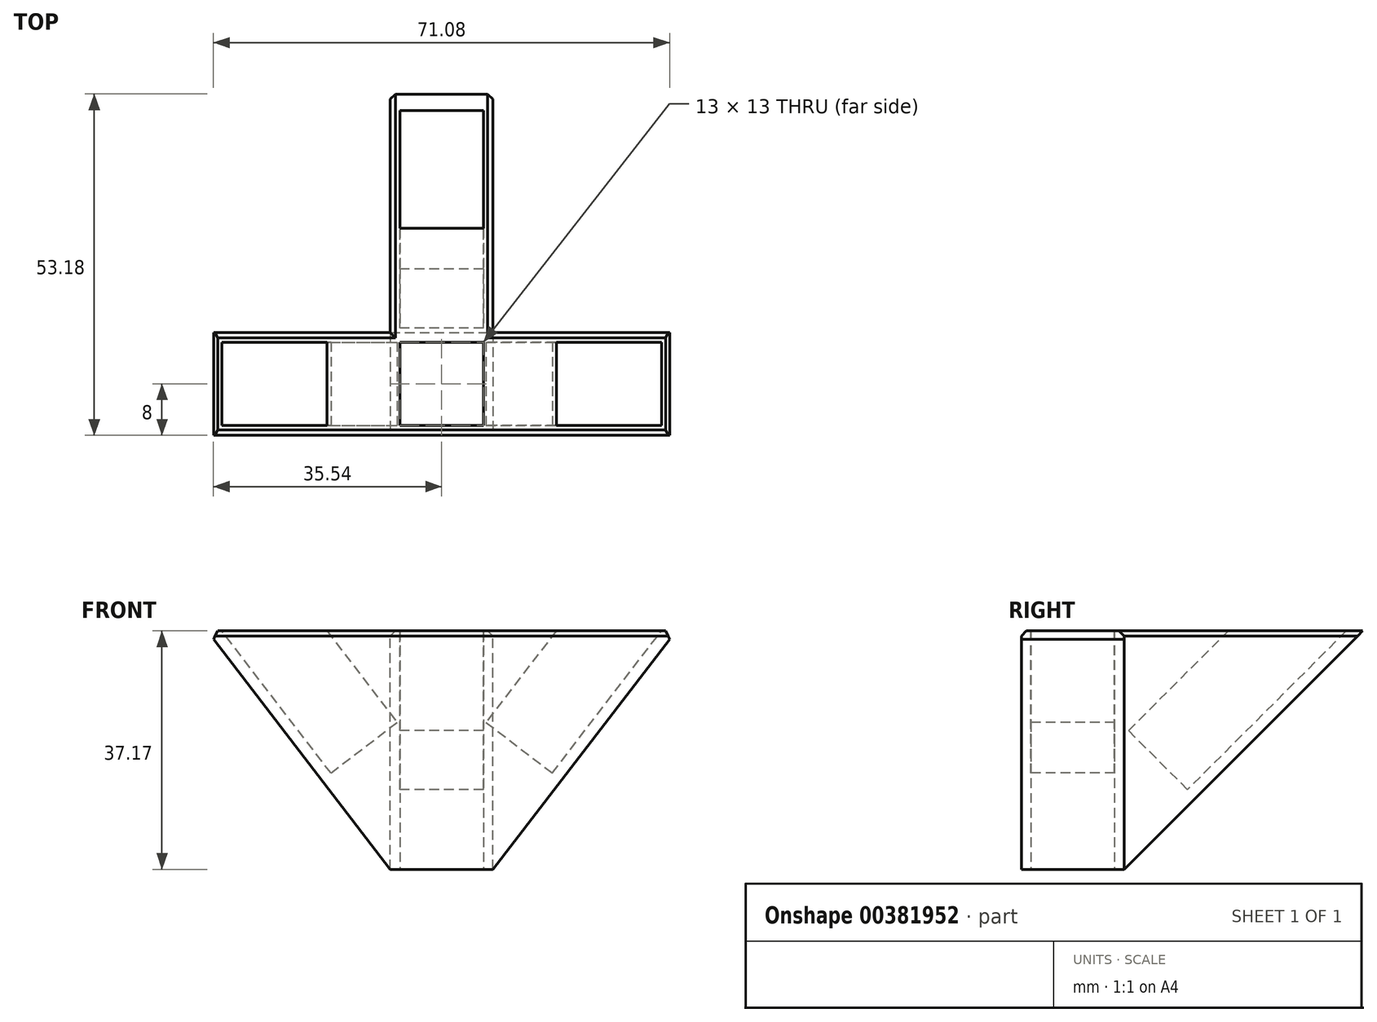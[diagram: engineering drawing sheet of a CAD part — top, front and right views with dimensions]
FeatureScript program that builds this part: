
annotation { "Feature Type Name" : "Feature", "Feature Type Description" : "" }
export const myFeature = defineFeature(function(context is Context, id is Id, definition is map)
    precondition{}
    {
        {
            var Q0;
            Q0=qCreatedBy(makeId("Front.planeOp"),FACE);
            var sketch = newSketch(context, id + "F0", { "sketchPlane" : qUnion([Q0])});
            skLineSegment(sketch, "E0", {"start": v(0, 0) * mm, "end": v(-36.53, 47.6) * mm});
            skLineSegment(sketch, "E1", {"start": v(-36.53, 47.6) * mm, "end": v(36.53, 47.6) * mm});
            skLineSegment(sketch, "E2", {"start": v(36.53, 47.6) * mm, "end": v(0, 0) * mm});
            skSolve(sketch);
        }
        {
            var Q0;
            Q0 = qSketchRegion(id + "F0", true);
            extrude(context, id + "F1", {"entities" : qUnion([Q0]), "depth" : 16 * mm});
        }
        {
            var Q0;
            Q0=qCreatedBy(makeId("Right.planeOp"),FACE);
            var sketch = newSketch(context, id + "F2", { "sketchPlane" : qUnion([Q0])});
            skLineSegment(sketch, "E3", {"start": v(0, 0) * mm, "end": v(47.6, 47.6) * mm});
            skPoint(sketch, "E4.0", {"position": v(0, 47.6) * mm});
            skLineSegment(sketch, "E5", {"start": v(0, 0) * mm, "end": v(0, 47.6) * mm});
            skLineSegment(sketch, "E6", {"start": v(0, 47.6) * mm, "end": v(47.6, 47.6) * mm});
            skSolve(sketch);
        }
        {
            var Q0;
            Q0 = qSketchRegion(id + "F2", true);
            extrude(context, id + "F3", {"entities" : qUnion([Q0]), "operationType" : NewBodyOperationType.ADD, "depth" : 8 * mm, "hasSecondDirection" : true, "secondDirectionOppositeDirection" : true, "secondDirectionDepth" : 8 * mm});
        }
        {
            var Q0;
            Q0=makeQuery(id+"F1.opExtrude","CAP_FACE",FACE,{"disambiguationData":[OSD([sQuery(id+"F0.wireOp",EDGE,"E0"),sQuery(id+"F0.wireOp",EDGE,"E1"),sQuery(id+"F0.wireOp",EDGE,"E2")])],"isStart":false});
            var sketch = newSketch(context, id + "F4", { "sketchPlane" : qUnion([Q0])});
            skLineSegment(sketch, "E7.0", {"start": v(-8, 0) * mm, "end": v(-8, 10.43) * mm});
            skLineSegment(sketch, "E8.0", {"start": v(8, 0) * mm, "end": v(8, 10.43) * mm});
            skLineSegment(sketch, "E9.bottom", {"start": v(-8, 0) * mm, "end": v(8, 0) * mm});
            skLineSegment(sketch, "E9.top", {"start": v(-8, 10.43) * mm, "end": v(8, 10.43) * mm});
            skSolve(sketch);
        }
        {
            var Q0;
            Q0 = qSketchRegion(id + "F4", true);
            extrude(context, id + "F5", {"entities" : qUnion([Q0]), "operationType" : NewBodyOperationType.REMOVE, "oppositeDirection" : true, "depth" : 45.4 * mm});
        }
        {
            var Q0;
            Q0=makeQuery(id+"F3.opExtrude","CAP_FACE",FACE,{"disambiguationData":[OSD([sQuery(id+"F2.wireOp",EDGE,"E3"),sQuery(id+"F2.wireOp",EDGE,"E5"),sQuery(id+"F2.wireOp",EDGE,"E6")])],"isStart":false});
            var sketch = newSketch(context, id + "F6", { "sketchPlane" : qUnion([Q0])});
            skLineSegment(sketch, "E10", {"start": v(0, 10.43) * mm, "end": v(37.18, 47.6) * mm});
            skLineSegment(sketch, "E11", {"start": v(37.18, 47.6) * mm, "end": v(47.6, 47.6) * mm});
            skLineSegment(sketch, "E12", {"start": v(47.6, 47.6) * mm, "end": v(10.43, 10.43) * mm});
            skLineSegment(sketch, "E13", {"start": v(10.43, 10.43) * mm, "end": v(0, 10.43) * mm});
            skSolve(sketch);
        }
        {
            var Q0;
            Q0 = qSketchRegion(id + "F6", true);
            extrude(context, id + "F7", {"entities" : qUnion([Q0]), "operationType" : NewBodyOperationType.REMOVE, "oppositeDirection" : true, "depth" : 25 * mm});
        }
        {
            var Q0;
            Q0=makeQuery(id+"F1.opExtrude","CAP_FACE",FACE,{"disambiguationData":[OSD([sQuery(id+"F0.wireOp",EDGE,"E0"),sQuery(id+"F0.wireOp",EDGE,"E1"),sQuery(id+"F0.wireOp",EDGE,"E2")])],"isStart":false});
            var sketch = newSketch(context, id + "F8", { "sketchPlane" : qUnion([Q0])});
            skLineSegment(sketch, "E14", {"start": v(-17.24, 25.43) * mm, "end": v(-54.33, 73.76) * mm});
            skLineSegment(sketch, "E15", {"start": v(-54.33, 73.76) * mm, "end": v(-44.01, 81.67) * mm});
            skLineSegment(sketch, "E16", {"start": v(-44.01, 81.67) * mm, "end": v(-6.93, 33.34) * mm});
            skLineSegment(sketch, "E17", {"start": v(-17.24, 25.43) * mm, "end": v(-6.93, 33.34) * mm});
            skLineSegment(sketch, "E18", {"start": v(17.24, 25.43) * mm, "end": v(53.12, 72.18) * mm});
            skLineSegment(sketch, "E19", {"start": v(53.12, 72.18) * mm, "end": v(42.8, 80.1) * mm});
            skLineSegment(sketch, "E20", {"start": v(42.8, 80.1) * mm, "end": v(6.93, 33.34) * mm});
            skLineSegment(sketch, "E21", {"start": v(6.93, 33.34) * mm, "end": v(17.24, 25.43) * mm});
            skSolve(sketch);
        }
        {
            var Q0;
            Q0 = qSketchRegion(id + "F8", true);
            extrude(context, id + "F9", {"entities" : qUnion([Q0]), "operationType" : NewBodyOperationType.REMOVE, "oppositeDirection" : true, "depth" : 14.5 * mm, "hasSecondDirection" : true, "secondDirectionOppositeDirection" : true, "secondDirectionDepth" : 1.5 * mm});
        }
        {
            var Q0;
            Q0=makeQuery(id+"F3.opExtrude","CAP_FACE",FACE,{"disambiguationData":[OSD([sQuery(id+"F2.wireOp",EDGE,"E3"),sQuery(id+"F2.wireOp",EDGE,"E5"),sQuery(id+"F2.wireOp",EDGE,"E6")])],"isStart":true});
            var sketch = newSketch(context, id + "F10", { "sketchPlane" : qUnion([Q0])});
            skLineSegment(sketch, "E22", {"start": v(-34.63, 47.6) * mm, "end": v(-9.88, 22.85) * mm});
            skLineSegment(sketch, "E23", {"start": v(-9.88, 22.85) * mm, "end": v(-0.69, 32.04) * mm});
            skLineSegment(sketch, "E24", {"start": v(-0.69, 32.04) * mm, "end": v(-16.25, 47.6) * mm});
            skLineSegment(sketch, "E25", {"start": v(-16.25, 47.6) * mm, "end": v(-34.63, 47.6) * mm});
            skSolve(sketch);
        }
        {
            var Q0;
            Q0 = qSketchRegion(id + "F10", true);
            extrude(context, id + "F11", {"entities" : qUnion([Q0]), "operationType" : NewBodyOperationType.REMOVE, "oppositeDirection" : true, "depth" : 14.5 * mm, "hasSecondDirection" : true, "secondDirectionOppositeDirection" : true, "secondDirectionDepth" : 1.5 * mm});
        }
        {
            var Q0;
            Q0=makeQuery(id+"F5.boolean.opBoolean","COPY",FACE,{"derivedFrom":makeQuery(id+"F5.opExtrude","SWEPT_FACE",FACE,{"disambiguationData":[OSD([sQuery(id+"F4.wireOp",EDGE,"E9.top")])]})});
            var sketch = newSketch(context, id + "F12", { "sketchPlane" : qUnion([Q0])});
            skLineSegment(sketch, "E26.bottom", {"start": v(6.5, 14.5) * mm, "end": v(-6.5, 14.5) * mm});
            skLineSegment(sketch, "E26.top", {"start": v(6.5, 1.5) * mm, "end": v(-6.5, 1.5) * mm});
            skLineSegment(sketch, "E26.left", {"start": v(6.5, 14.5) * mm, "end": v(6.5, 1.5) * mm});
            skLineSegment(sketch, "E26.right", {"start": v(-6.5, 14.5) * mm, "end": v(-6.5, 1.5) * mm});
            skPoint(sketch, "E26.middle", {"position": v(0, 8) * mm});
            skPoint(sketch, "E26.middle.positionSnap0", {"position": v(8, 8) * mm});
            skPoint(sketch, "E26.middle.positionSnap1", {"position": v(0, 16) * mm});
            skPoint(sketch, "E26.centerSnap0", {"position": v(8, 8) * mm});
            skPoint(sketch, "E26.centerSnap1", {"position": v(0, 16) * mm});
            skSolve(sketch);
        }
        {
            var Q0;
            Q0 = qSketchRegion(id + "F12", true);
            extrude(context, id + "F13", {"entities" : qUnion([Q0]), "operationType" : NewBodyOperationType.REMOVE, "oppositeDirection" : true, "depth" : 45.8 * mm});
        }
        {
            var Q0;
            Q0=makeQuery(id+"F1.opExtrude","SWEPT_EDGE",EDGE,{"disambiguationData":[OSD([sQuery(id+"F0.wireOp",EDGE,"E0"),sQuery(id+"F0.wireOp",EDGE,"E1")])]});
            var Q1;
            {var subQ1=sQuery(id+"F0.wireOp",EDGE,"E1");var subQ2=sQuery(id+"F0.wireOp",EDGE,"E0");Q1=makeQuery(id+"F3.boolean.opBoolean","SPLIT",EDGE,{"disambiguationData":[TD([makeQuery(id+"F1.opExtrude","SWEPT_FACE",FACE,{"disambiguationData":[OSD([subQ2])]})])],"derivedFrom":makeQuery(id+"F1.opExtrude","CAP_EDGE",EDGE,{"disambiguationData":[OSD([subQ1])],"isStart":true})});}
            var Q2;
            Q2=makeQuery(id+"F1.opExtrude","CAP_EDGE",EDGE,{"disambiguationData":[OSD([sQuery(id+"F0.wireOp",EDGE,"E1")])],"isStart":false});
            var Q3;
            Q3=makeQuery(id+"F1.opExtrude","SWEPT_EDGE",EDGE,{"disambiguationData":[OSD([sQuery(id+"F0.wireOp",EDGE,"E1"),sQuery(id+"F0.wireOp",EDGE,"E2")])]});
            var Q4;
            {var subQ1=sQuery(id+"F0.wireOp",EDGE,"E1");var subQ2=sQuery(id+"F0.wireOp",EDGE,"E2");Q4=makeQuery(id+"F3.boolean.opBoolean","SPLIT",EDGE,{"disambiguationData":[TD([makeQuery(id+"F1.opExtrude","SWEPT_FACE",FACE,{"disambiguationData":[OSD([subQ2])]})])],"derivedFrom":makeQuery(id+"F1.opExtrude","CAP_EDGE",EDGE,{"disambiguationData":[OSD([subQ1])],"isStart":true})});}
            var Q5;
            Q5=makeQuery(id+"F3.opExtrude","CAP_EDGE",EDGE,{"disambiguationData":[OSD([sQuery(id+"F2.wireOp",EDGE,"E6")])],"isStart":false});
            var Q6;
            Q6=makeQuery(id+"F3.opExtrude","CAP_EDGE",EDGE,{"disambiguationData":[OSD([sQuery(id+"F2.wireOp",EDGE,"E6")])],"isStart":true});
            var Q7;
            Q7=makeQuery(id+"F7.boolean.opBoolean","COPY",EDGE,{"derivedFrom":makeQuery(id+"F7.opExtrude","SWEPT_EDGE",EDGE,{"disambiguationData":[OSD([sQuery(id+"F2.wireOp",EDGE,"E6"),sQuery(id+"F6.wireOp",EDGE,"E10"),sQuery(id+"F6.wireOp",EDGE,"E11")])]})});
            chamfer(context, id + "F14", {"entities" : qUnion([Q0, Q1, Q2, Q3, Q4, Q5, Q6, Q7]), "width" : 0.8 * mm, "tangentPropagation" : true});
        }
    });
